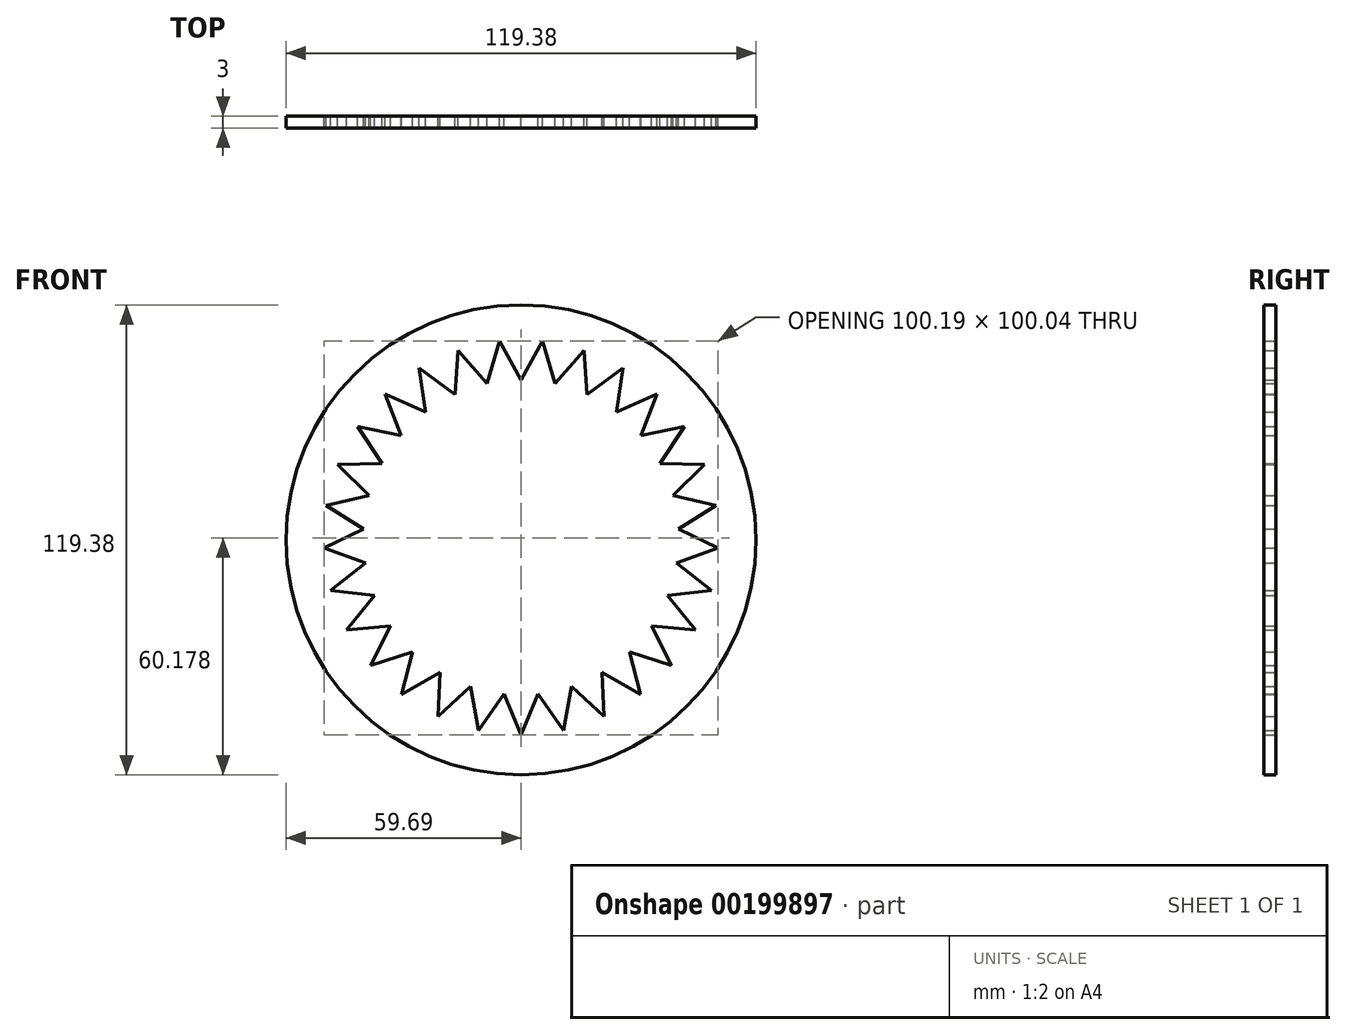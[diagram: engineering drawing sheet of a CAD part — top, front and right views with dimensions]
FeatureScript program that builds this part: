
annotation { "Feature Type Name" : "Feature", "Feature Type Description" : "" }
export const myFeature = defineFeature(function(context is Context, id is Id, definition is map)
    precondition{}
    {
        {
            var Q0;
            Q0=qCreatedBy(makeId("Front.planeOp"),FACE);
            var sketch = newSketch(context, id + "F0", { "sketchPlane" : qUnion([Q0])});
            skLineSegment(sketch, "E0", {"start": v(0, 40.64) * mm, "end": v(5.42, 50.5) * mm});
            skLineSegment(sketch, "E1", {"start": v(0, 40.64) * mm, "end": v(-5.42, 50.5) * mm});
            skLineSegment(sketch, "E2.1.0", {"start": v(-8.6, 39.7) * mm, "end": v(-5.42, 50.5) * mm});
            skLineSegment(sketch, "E2.1.1", {"start": v(-8.6, 39.7) * mm, "end": v(-16.02, 48.18) * mm});
            skLineSegment(sketch, "E2.2.0", {"start": v(-16.8, 36.94) * mm, "end": v(-16.02, 48.18) * mm});
            skLineSegment(sketch, "E2.2.1", {"start": v(-16.8, 36.94) * mm, "end": v(-25.86, 43.62) * mm});
            skLineSegment(sketch, "E2.3.0", {"start": v(-24.21, 32.48) * mm, "end": v(-25.86, 43.62) * mm});
            skLineSegment(sketch, "E2.3.1", {"start": v(-24.21, 32.48) * mm, "end": v(-34.5, 37.06) * mm});
            skLineSegment(sketch, "E2.4.0", {"start": v(-30.5, 26.53) * mm, "end": v(-34.5, 37.06) * mm});
            skLineSegment(sketch, "E2.4.1", {"start": v(-30.5, 26.53) * mm, "end": v(-41.52, 28.79) * mm});
            skLineSegment(sketch, "E2.5.0", {"start": v(-35.35, 19.37) * mm, "end": v(-41.52, 28.79) * mm});
            skLineSegment(sketch, "E2.5.1", {"start": v(-35.35, 19.37) * mm, "end": v(-46.6, 19.2) * mm});
            skLineSegment(sketch, "E2.6.0", {"start": v(-38.55, 11.34) * mm, "end": v(-46.6, 19.2) * mm});
            skLineSegment(sketch, "E2.6.1", {"start": v(-38.55, 11.34) * mm, "end": v(-49.5, 8.75) * mm});
            skLineSegment(sketch, "E2.7.0", {"start": v(-39.95, 2.8) * mm, "end": v(-49.5, 8.75) * mm});
            skLineSegment(sketch, "E2.7.1", {"start": v(-39.95, 2.8) * mm, "end": v(-50.1, -2.08) * mm});
            skLineSegment(sketch, "E2.8.0", {"start": v(-39.48, -5.84) * mm, "end": v(-50.1, -2.08) * mm});
            skLineSegment(sketch, "E2.8.1", {"start": v(-39.48, -5.84) * mm, "end": v(-48.34, -12.79) * mm});
            skLineSegment(sketch, "E2.9.0", {"start": v(-37.16, -14.17) * mm, "end": v(-48.34, -12.79) * mm});
            skLineSegment(sketch, "E2.9.1", {"start": v(-37.16, -14.17) * mm, "end": v(-44.32, -22.86) * mm});
            skLineSegment(sketch, "E2.10.0", {"start": v(-33.11, -21.82) * mm, "end": v(-44.32, -22.86) * mm});
            skLineSegment(sketch, "E2.10.1", {"start": v(-33.11, -21.82) * mm, "end": v(-38.24, -31.84) * mm});
            skLineSegment(sketch, "E2.11.0", {"start": v(-27.51, -28.4) * mm, "end": v(-38.24, -31.84) * mm});
            skLineSegment(sketch, "E2.11.1", {"start": v(-27.51, -28.4) * mm, "end": v(-30.36, -39.3) * mm});
            skLineSegment(sketch, "E2.12.0", {"start": v(-20.62, -33.64) * mm, "end": v(-30.36, -39.3) * mm});
            skLineSegment(sketch, "E2.12.1", {"start": v(-20.62, -33.64) * mm, "end": v(-21.07, -44.9) * mm});
            skLineSegment(sketch, "E2.13.0", {"start": v(-12.77, -37.28) * mm, "end": v(-21.07, -44.9) * mm});
            skLineSegment(sketch, "E2.13.1", {"start": v(-12.77, -37.28) * mm, "end": v(-10.78, -48.36) * mm});
            skLineSegment(sketch, "E2.14.0", {"start": v(-4.33, -39.14) * mm, "end": v(-10.78, -48.36) * mm});
            skLineSegment(sketch, "E2.14.1", {"start": v(-4.33, -39.14) * mm, "end": v(0, -49.53) * mm});
            skLineSegment(sketch, "E2.15.0", {"start": v(4.33, -39.14) * mm, "end": v(0, -49.53) * mm});
            skLineSegment(sketch, "E2.15.1", {"start": v(4.33, -39.14) * mm, "end": v(10.78, -48.36) * mm});
            skLineSegment(sketch, "E2.16.0", {"start": v(12.77, -37.28) * mm, "end": v(10.78, -48.36) * mm});
            skLineSegment(sketch, "E2.16.1", {"start": v(12.77, -37.28) * mm, "end": v(21.07, -44.9) * mm});
            skLineSegment(sketch, "E2.17.0", {"start": v(20.62, -33.64) * mm, "end": v(21.07, -44.9) * mm});
            skLineSegment(sketch, "E2.17.1", {"start": v(20.62, -33.64) * mm, "end": v(30.36, -39.3) * mm});
            skLineSegment(sketch, "E2.18.0", {"start": v(27.51, -28.4) * mm, "end": v(30.36, -39.3) * mm});
            skLineSegment(sketch, "E2.18.1", {"start": v(27.51, -28.4) * mm, "end": v(38.24, -31.84) * mm});
            skLineSegment(sketch, "E2.19.0", {"start": v(33.11, -21.82) * mm, "end": v(38.24, -31.84) * mm});
            skLineSegment(sketch, "E2.19.1", {"start": v(33.11, -21.82) * mm, "end": v(44.32, -22.86) * mm});
            skLineSegment(sketch, "E2.20.0", {"start": v(37.16, -14.17) * mm, "end": v(44.32, -22.86) * mm});
            skLineSegment(sketch, "E2.20.1", {"start": v(37.16, -14.17) * mm, "end": v(48.34, -12.79) * mm});
            skLineSegment(sketch, "E2.21.0", {"start": v(39.48, -5.84) * mm, "end": v(48.34, -12.79) * mm});
            skLineSegment(sketch, "E2.21.1", {"start": v(39.48, -5.84) * mm, "end": v(50.1, -2.08) * mm});
            skLineSegment(sketch, "E2.22.0", {"start": v(39.95, 2.8) * mm, "end": v(50.1, -2.08) * mm});
            skLineSegment(sketch, "E2.22.1", {"start": v(39.95, 2.8) * mm, "end": v(49.5, 8.75) * mm});
            skLineSegment(sketch, "E2.23.0", {"start": v(38.55, 11.34) * mm, "end": v(49.5, 8.75) * mm});
            skLineSegment(sketch, "E2.23.1", {"start": v(38.55, 11.34) * mm, "end": v(46.6, 19.2) * mm});
            skLineSegment(sketch, "E2.24.0", {"start": v(35.35, 19.37) * mm, "end": v(46.6, 19.2) * mm});
            skLineSegment(sketch, "E2.24.1", {"start": v(35.35, 19.37) * mm, "end": v(41.52, 28.79) * mm});
            skLineSegment(sketch, "E2.25.0", {"start": v(30.5, 26.53) * mm, "end": v(41.52, 28.79) * mm});
            skLineSegment(sketch, "E2.25.1", {"start": v(30.5, 26.53) * mm, "end": v(34.5, 37.06) * mm});
            skLineSegment(sketch, "E2.26.0", {"start": v(24.21, 32.48) * mm, "end": v(34.5, 37.06) * mm});
            skLineSegment(sketch, "E2.26.1", {"start": v(24.21, 32.48) * mm, "end": v(25.86, 43.62) * mm});
            skLineSegment(sketch, "E2.27.0", {"start": v(16.8, 36.94) * mm, "end": v(25.86, 43.62) * mm});
            skLineSegment(sketch, "E2.27.1", {"start": v(16.8, 36.94) * mm, "end": v(16.02, 48.18) * mm});
            skLineSegment(sketch, "E2.28.0", {"start": v(8.6, 39.7) * mm, "end": v(16.02, 48.18) * mm});
            skLineSegment(sketch, "E2.28.1", {"start": v(8.6, 39.7) * mm, "end": v(5.42, 50.5) * mm});
            skCircle(sketch, "E3", {"center": v(0, 0) * mm, "radius": 59.7 * mm});
            skCircle(sketch, "E4.MirrorC", {"center": v(-110.2, 3.52) * mm, "radius": 0.97 * mm});
            skLineSegment(sketch, "E5", {"start": v(0, 25.4) * mm, "end": v(0, 15.5) * mm});
            skLineSegment(sketch, "E6", {"start": v(0, 15.5) * mm, "end": v(5.6, 24.77) * mm});
            skLineSegment(sketch, "E7.MirrorCS", {"start": v(0, 15.5) * mm, "end": v(-5.6, 24.77) * mm});
            skLineSegment(sketch, "E8.1.0", {"start": v(-6.51, 14.12) * mm, "end": v(-5.5, 24.91) * mm});
            skLineSegment(sketch, "E8.1.1", {"start": v(-6.51, 14.12) * mm, "end": v(-15.59, 20.05) * mm});
            skLineSegment(sketch, "E8.2.0", {"start": v(-11.79, 10.06) * mm, "end": v(-15.55, 20.23) * mm});
            skLineSegment(sketch, "E8.2.1", {"start": v(-11.79, 10.06) * mm, "end": v(-22.54, 11.47) * mm});
            skLineSegment(sketch, "E8.3.0", {"start": v(-14.77, 4.11) * mm, "end": v(-22.58, 11.64) * mm});
            skLineSegment(sketch, "E8.3.1", {"start": v(-14.77, 4.11) * mm, "end": v(-25.07, 0.72) * mm});
            skLineSegment(sketch, "E8.4.0", {"start": v(-14.89, -2.54) * mm, "end": v(-25.18, 0.86) * mm});
            skLineSegment(sketch, "E8.4.1", {"start": v(-14.89, -2.54) * mm, "end": v(-22.69, -10.07) * mm});
            skLineSegment(sketch, "E8.5.0", {"start": v(-12.1, -8.59) * mm, "end": v(-22.85, -10) * mm});
            skLineSegment(sketch, "E8.5.1", {"start": v(-12.1, -8.59) * mm, "end": v(-15.86, -18.75) * mm});
            skLineSegment(sketch, "E8.6.0", {"start": v(-6.97, -12.82) * mm, "end": v(-16.04, -18.75) * mm});
            skLineSegment(sketch, "E8.6.1", {"start": v(-6.97, -12.82) * mm, "end": v(-5.95, -23.62) * mm});
            skLineSegment(sketch, "E8.7.0", {"start": v(-0.5, -14.41) * mm, "end": v(-6.1, -23.7) * mm});
            skLineSegment(sketch, "E8.7.1", {"start": v(-0.5, -14.41) * mm, "end": v(5.1, -23.7) * mm});
            skLineSegment(sketch, "E8.8.0", {"start": v(6, -13.04) * mm, "end": v(4.99, -23.83) * mm});
            skLineSegment(sketch, "E8.8.1", {"start": v(6, -13.04) * mm, "end": v(15.08, -18.97) * mm});
            skLineSegment(sketch, "E8.9.0", {"start": v(11.28, -8.98) * mm, "end": v(15.05, -19.15) * mm});
            skLineSegment(sketch, "E8.9.1", {"start": v(11.28, -8.98) * mm, "end": v(22.03, -10.39) * mm});
            skLineSegment(sketch, "E8.10.0", {"start": v(14.27, -3.03) * mm, "end": v(22.07, -10.56) * mm});
            skLineSegment(sketch, "E8.10.1", {"start": v(14.27, -3.03) * mm, "end": v(24.57, 0.36) * mm});
            skLineSegment(sketch, "E8.11.0", {"start": v(14.38, 3.62) * mm, "end": v(24.68, 0.23) * mm});
            skLineSegment(sketch, "E8.11.1", {"start": v(14.38, 3.62) * mm, "end": v(22.18, 11.15) * mm});
            skLineSegment(sketch, "E8.12.0", {"start": v(11.6, 9.67) * mm, "end": v(22.35, 11.07) * mm});
            skLineSegment(sketch, "E8.12.1", {"start": v(11.6, 9.67) * mm, "end": v(15.36, 19.83) * mm});
            skLineSegment(sketch, "E8.13.0", {"start": v(6.46, 13.9) * mm, "end": v(15.54, 19.83) * mm});
            skLineSegment(sketch, "E8.13.1", {"start": v(6.46, 13.9) * mm, "end": v(5.44, 24.7) * mm});
            skSolve(sketch);
        }
        {
            var Q0;
            Q0=makeQuery(id+"F0.imprint","IMPRINT",FACE,{"disambiguationData":[TD([[makeQuery(id+"F0.imprint","IMPRINT",EDGE,{"derivedFrom":sQuery(id+"F0.wireOp",EDGE,"E0")}),1.0]])]});
            var Q1;
            Q1=makeQuery(id+"F0.imprint","IMPRINT",FACE,{"disambiguationData":[TD([[makeQuery(id+"F0.imprint","IMPRINT",EDGE,{"derivedFrom":sQuery(id+"F0.wireOp",EDGE,"DRvC4sdE-3LT7-3dlg-faxH-AgBNUoLRJLBF")}),-1.0]])]});
            extrude(context, id + "F1", {"entities" : qUnion([Q0, Q1]), "depth" : 3 * mm});
        }
    });
